FCSTD DOCUMENT  (FreeCAD 0.19R0.19.2)
Label: v0_05
License: All rights reserved
LicenseURL: http://en.wikipedia.org/wiki/All_rights_reserved
objects: Sketcher::SketchObject×1
note: 1 computed .brp shape members not serialized (recipe doc carries the construction recipe); baked Part::Feature solids carry a one-line shape summary decoded from their .brp

FEATURE [Sketcher::SketchObject] Sketch
  FullyConstrained = false
  sketch-geometry (42):
    g0: LineSegment StartX=-7.5 StartY=-26.2 StartZ=0 EndX=-27.5 EndY=-26.2 EndZ=0
    g1: LineSegment StartX=-20 StartY=0 StartZ=0 EndX=0 EndY=0 EndZ=0
    g2: LineSegment StartX=-25 StartY=-3.1 StartZ=0 EndX=-20 EndY=-3.1 EndZ=0
    g3: LineSegment StartX=-27.5 StartY=-8.1 StartZ=0 EndX=-27.5 EndY=-11.85 EndZ=0
    g4: ArcOfCircle CenterX=-25 CenterY=-8.1 CenterZ=0 NormalX=0 NormalY=0 NormalZ=1 AngleXU=0 Radius=2.5 StartAngle=1.5708 EndAngle=3.14159
    g5: LineSegment StartX=-25 StartY=-14.35 StartZ=0 EndX=-22.5 EndY=-14.35 EndZ=0
    g6: ArcOfCircle CenterX=-25 CenterY=-11.85 CenterZ=0 NormalX=0 NormalY=0 NormalZ=1 AngleXU=0 Radius=2.5 StartAngle=3.14159 EndAngle=4.71239
    g7: LineSegment StartX=-22.5 StartY=-14.35 StartZ=0 EndX=-22.5 EndY=-11.85 EndZ=0
    g8: LineSegment StartX=-22.5 StartY=-11.85 StartZ=0 EndX=-20 EndY=-11.85 EndZ=0
    g9: ArcOfCircle CenterX=-20 CenterY=-14.35 CenterZ=0 NormalX=0 NormalY=0 NormalZ=1 AngleXU=0 Radius=2.5 StartAngle=8e-16 EndAngle=1.5708
    g10: LineSegment StartX=-17.5 StartY=-14.35 StartZ=0 EndX=-17.5 EndY=-18.1 EndZ=0
    g11: ArcOfCircle CenterX=-20 CenterY=-18.1 CenterZ=0 NormalX=0 NormalY=0 NormalZ=1 AngleXU=0 Radius=2.5 StartAngle=4.71239 EndAngle=6.28319
    g12: LineSegment StartX=-22.5 StartY=-20.6 StartZ=0 EndX=-20 EndY=-20.6 EndZ=0
    g13: LineSegment StartX=-22.5 StartY=-20.6 StartZ=0 EndX=-22.5 EndY=-23.1 EndZ=0
    g14: LineSegment StartX=-27.5 StartY=-23.1 StartZ=0 EndX=-22.5 EndY=-23.1 EndZ=0
    g15: LineSegment StartX=-27.5 StartY=-23.1 StartZ=0 EndX=-27.5 EndY=-26.2 EndZ=0
    g16: LineSegment StartX=-25 StartY=-8.1 StartZ=0 EndX=-25 EndY=-7.9 EndZ=0
    g17: LineSegment StartX=-25.2 StartY=-7.9 StartZ=0 EndX=-25 EndY=-7.9 EndZ=0
    g18: LineSegment StartX=-20 StartY=-14.35 StartZ=0 EndX=-20 EndY=-14.55 EndZ=0
    g19: LineSegment StartX=-20 StartY=-14.55 StartZ=0 EndX=-20.2 EndY=-14.55 EndZ=0
    g20: LineSegment StartX=-20 StartY=-18.1 StartZ=0 EndX=-20 EndY=-17.9 EndZ=0
    g21: LineSegment StartX=-20 StartY=-17.9 StartZ=0 EndX=-20.2 EndY=-17.9 EndZ=0
    g22: ArcOfCircle CenterX=-20 CenterY=-14.35 CenterZ=0 NormalX=0 NormalY=0 NormalZ=1 AngleXU=0 Radius=2.3 StartAngle=8e-16 EndAngle=1.5708
    g23: ArcOfCircle CenterX=-20 CenterY=-18.1 CenterZ=0 NormalX=0 NormalY=0 NormalZ=1 AngleXU=0 Radius=2.3 StartAngle=4.71239 EndAngle=6.28319
    g24: LineSegment StartX=-20 StartY=-20.4 StartZ=0 EndX=-22.7 EndY=-20.4 EndZ=0
    g25: LineSegment StartX=-22.7 StartY=-23.1 StartZ=0 EndX=-22.5 EndY=-23.1 EndZ=0
    g26: LineSegment StartX=-22.7 StartY=-22.9 StartZ=0 EndX=-22.7 EndY=-20.4 EndZ=0
    g27: LineSegment StartX=-17.7 StartY=-14.35 StartZ=0 EndX=-17.7 EndY=-18.1 EndZ=0
    g28: LineSegment StartX=-25.2 StartY=-5.40742 StartZ=0 EndX=-25.2 EndY=-2.9 EndZ=0
    g29: LineSegment StartX=-25.2 StartY=-2.9 StartZ=0 EndX=-20.2 EndY=-2.9 EndZ=0
    g30: LineSegment StartX=-20.2 StartY=-2.9 StartZ=0 EndX=-20.2 EndY=0 EndZ=0
    g31: ArcOfCircle CenterX=-25 CenterY=-8.1 CenterZ=0 NormalX=0 NormalY=0 NormalZ=1 AngleXU=0 Radius=2.7 StartAngle=1.64494 EndAngle=3.14159
    g32: ArcOfCircle CenterX=-25 CenterY=-11.85 CenterZ=0 NormalX=0 NormalY=0 NormalZ=1 AngleXU=0 Radius=2.7 StartAngle=3.14159 EndAngle=4.71239
    g33: LineSegment StartX=-27.7 StartY=-8.1 StartZ=0 EndX=-27.7 EndY=-11.85 EndZ=0
    g34: LineSegment StartX=-25 StartY=-14.55 StartZ=0 EndX=-22.3 EndY=-14.55 EndZ=0
    g35: LineSegment StartX=-22.5 StartY=-11.85 StartZ=0 EndX=-22.5 EndY=-12.05 EndZ=0
    g36: LineSegment StartX=-22.3 StartY=-12.05 StartZ=0 EndX=-22.3 EndY=-14.55 EndZ=0
    g37: LineSegment StartX=-22.3 StartY=-12.05 StartZ=0 EndX=-20 EndY=-12.05 EndZ=0
    g38: LineSegment StartX=-27.7 StartY=-22.9 StartZ=0 EndX=-22.7 EndY=-22.9 EndZ=0
    g39: LineSegment StartX=-27.7 StartY=-26.2 StartZ=0 EndX=-27.5 EndY=-26.2 EndZ=0
    g40: LineSegment StartX=-27.7 StartY=-22.9 StartZ=0 EndX=-27.7 EndY=-26.2 EndZ=0
    g41: LineSegment StartX=-142.5 StartY=0 StartZ=0 EndX=-20.2 EndY=0 EndZ=0
  constraints (104):
    c: Horizontal(g0)
    c: Distance(g0) = 20
    c: Horizontal(g1)
    c: Distance(g1) = 20
    c: Horizontal(g2)
    c: Vertical(g3)
    c: Block(g4)
    c: Coincident(g3,g4)
    c: Horizontal(g5)
    c: Coincident(g6,g3)
    c: Block(g6)
    c: Block(g5)
    c: Vertical(g7)
    c: Coincident(g7,g5)
    c: Horizontal(g8)
    c: Coincident(g8,g7)
    c: Coincident(g9,g8)
    c: Vertical(g10)
    c: Block(g9)
    c: Coincident(g10,g9)
    c: Coincident(g11,g10)
    c: Block(g11)
    c: Horizontal(g12)
    c: Coincident(g12,g11)
    c: Vertical(g13)
    c: Coincident(g13,g12)
    c: Horizontal(g14)
    c: Coincident(g14,g13)
    c: Block(g2)
    c: Block(g14)
    c: Coincident(g15,g14)
    c: Coincident(g15,g0)
    c: Vertical(g15)
    c: Block(g15)
    c: Coincident(g16,g4)
    c: Vertical(g16)
    c: Distance(g16) = 0.2
    c: Horizontal(g17)
    c: Distance(g17) = 0.2
    c: Coincident(g17,g16)
    c: Vertical(g18)
    c: Distance(g18) = 0.2
    c: Coincident(g18,g9)
    c: Horizontal(g19)
    c: Distance(g19) = 0.2
    c: Coincident(g19,g18)
    c: Vertical(g20)
    c: Distance(g20) = 0.2
    c: Coincident(g20,g11)
    c: Horizontal(g21)
    c: Distance(g21) = 0.2
    c: Coincident(g21,g20)
    c: Coincident(g22,g9)
    c: Coincident(g23,g11)
    c: Block(g23)
    c: Block(g22)
    c: Coincident(g24,g23)
    c: Horizontal(g24)
    c: Horizontal(g25)
    c: Distance(g25) = 0.2
    c: Coincident(g25,g13)
    c: Vertical(g26)
    c: Coincident(g26,g24)
    c: Coincident(g27,g22)
    c: Coincident(g27,g23)
    c: Vertical(g27)
    c: Vertical(g28)
    c: Block(g28)
    c: Coincident(g29,g28)
    c: Horizontal(g29)
    c: Vertical(g30)
    c: Block(g30)
    c: Block(g29)
    c: Coincident(g31,g4)
    c: Coincident(g31,g28)
    c: Coincident(g32,g6)
    c: Block(g32)
    c: Coincident(g33,g31)
    c: Coincident(g33,g32)
    c: Vertical(g33)
    c: Block(g33)
    c: Coincident(g34,g32)
    c: Horizontal(g34)
    c: Vertical(g35)
    c: Distance(g35) = 0.2
    c: Coincident(g35,g7)
    c: Vertical(g36)
    c: Coincident(g36,g34)
    c: Block(g36)
    c: Coincident(g37,g22)
    c: Horizontal(g37)
    c: Block(g37)
    c: Coincident(g38,g26)
    c: Horizontal(g38)
    c: Block(g38)
    c: Horizontal(g39)
    c: Distance(g39) = 0.2
    c: Coincident(g39,g0)
    c: Coincident(g40,g38)
    c: Coincident(g40,g39)
    c: Vertical(g40)
    c: Horizontal(g41)
    c: Distance(g41) = 122.3
    c: Coincident(g41,g30)
